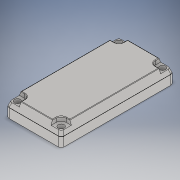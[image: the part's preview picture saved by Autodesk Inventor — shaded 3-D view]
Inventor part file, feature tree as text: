
AUTODESK INVENTOR PART (.ipt)
format: ipt  version: 2016 (Build 200138000, 138)  size: 259,072 bytes
history: native  units: mm
features: other x4, mirror x4, chamfer x4, extrude x3, fillet x2, sketch x2
ambient origin geometry x8: Origin, YZ Plane, XZ Plane, XY Plane, X Axis, Y Axis, Z Axis, Center Point
bodies: Body1 (feature_tree)
feature tree (19):
  other  "Sólido1"
  extrude  "Extrusión1"  Depth=40.6mm
  extrude  "Extrusión2"  Depth=0.2mm
  mirror  "Simetría1"
  mirror  "Simetría2"
  extrude  "Extrusión3"  Depth=0.2mm TaperAngle=0.0deg
  mirror  "Simetría3"
  mirror  "Simetría4"
  chamfer  "Chaflán1"  Distance=2.2mm
  chamfer  "Chaflán2"  Distance=2.2mm
  chamfer  "Chaflán3"  Distance=2.2mm
  chamfer  "Chaflán4"  Distance=1.5mm
  fillet  "Empalme1"  Radius=2.0mm
  fillet  "Empalme2"  Radius=2.0mm
  sketch  "Boceto1"  dims[d0=19.8mm d1=40.6mm]
  other  "Eje de trabajo1"
  other  "Eje de trabajo2"
  other  "Eje de trabajo3"
  sketch  "Boceto4"  dims[d2=6.4mm d3=0.0mm d6=3.6mm d8=1.5mm d9=0.0mm d10=2.2mm d11=2.2mm d12=2.2mm d13=1.5mm d14=0.0mm d15=3.0mm d16=2.0mm d17=3.490659mm d18=3.0mm d19=2.0mm d20=3.490659mm d21=3.0mm d22=2.0mm d23=3.490659mm d24=3.0mm d25=2.0mm d26=3.490659mm d27=1.0mm d28=0.2mm]
